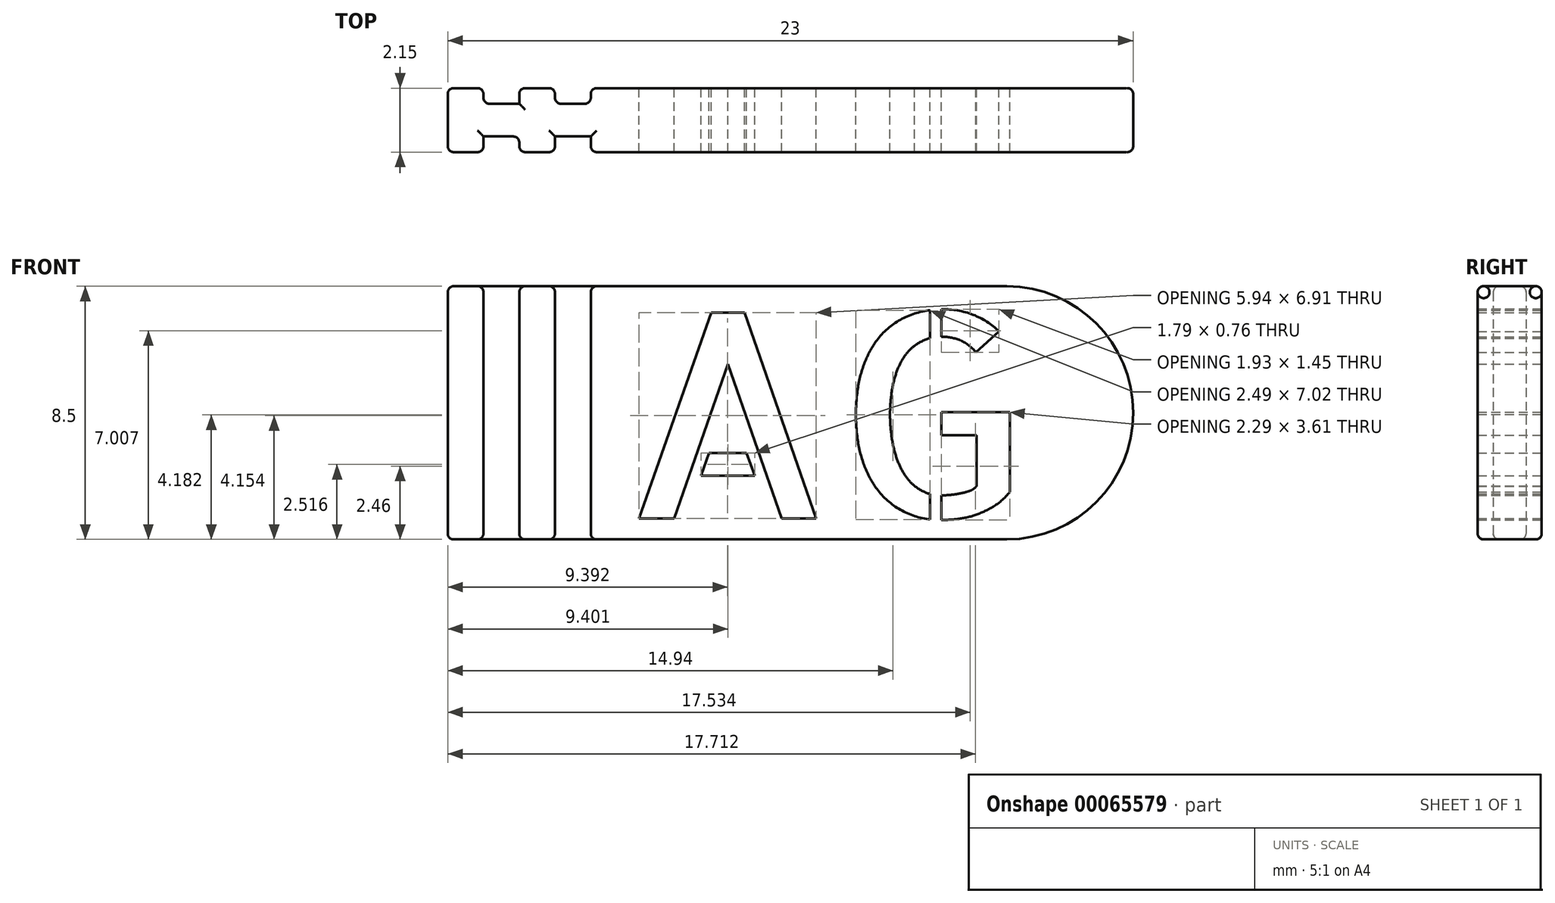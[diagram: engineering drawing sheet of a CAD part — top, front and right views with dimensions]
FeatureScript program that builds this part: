
annotation { "Feature Type Name" : "Feature", "Feature Type Description" : "" }
export const myFeature = defineFeature(function(context is Context, id is Id, definition is map)
    precondition{}
    {
        {
            var Q0;
            Q0=qCreatedBy(makeId("Front.planeOp"),FACE);
            var sketch = newSketch(context, id + "F0", { "sketchPlane" : qUnion([Q0])});
            skLineSegment(sketch, "E0.bottom", {"start": v(0, 0) * mm, "end": v(18.76, 0) * mm});
            skLineSegment(sketch, "E0.top", {"start": v(0, 8.5) * mm, "end": v(18.76, 8.5) * mm});
            skLineSegment(sketch, "E0.left", {"start": v(0, 0) * mm, "end": v(0, 8.5) * mm});
            skPoint(sketch, "E1.third.point", {"position": v(23, 4.25) * mm});
            skArc(sketch, "E2", {"start": v(18.74, 0) * mm, "mid": v(23, 4.25) * mm, "end": v(18.74, 8.5) * mm});
            skLineSegment(sketch, "E3.bottom", {"start": v(0, 8.5) * mm, "end": v(4.8, 8.5) * mm});
            skLineSegment(sketch, "E3.top", {"start": v(0, 0) * mm, "end": v(4.8, 0) * mm});
            skLineSegment(sketch, "E3.left", {"start": v(0, 8.5) * mm, "end": v(0, 0) * mm});
            skLineSegment(sketch, "E3.right", {"start": v(4.8, 8.5) * mm, "end": v(4.8, 0) * mm});
            skLineSegment(sketch, "E4.bottom", {"start": v(0, 8.5) * mm, "end": v(1.2, 8.5) * mm});
            skLineSegment(sketch, "E4.top", {"start": v(0, 0) * mm, "end": v(1.2, 0) * mm});
            skLineSegment(sketch, "E4.right", {"start": v(1.2, 8.5) * mm, "end": v(1.2, 0) * mm});
            skLineSegment(sketch, "E5.bottom", {"start": v(1.2, 8.5) * mm, "end": v(2.4, 8.5) * mm});
            skLineSegment(sketch, "E5.top", {"start": v(1.2, 0) * mm, "end": v(2.4, 0) * mm});
            skLineSegment(sketch, "E5.right", {"start": v(2.4, 8.5) * mm, "end": v(2.4, 0) * mm});
            skLineSegment(sketch, "E6.bottom", {"start": v(2.4, 8.5) * mm, "end": v(3.6, 8.5) * mm});
            skLineSegment(sketch, "E6.top", {"start": v(2.4, 0) * mm, "end": v(3.6, 0) * mm});
            skLineSegment(sketch, "E6.right", {"start": v(3.6, 8.5) * mm, "end": v(3.6, 0) * mm});
            skText(sketch, "E7", { "text": "AG", "fontName": "AllertaStencil-Regular.ttf"});
            const initialGuessF0  = {"E7": [0.00583, 0.0007, 1, 0, 0.00692]};
            skSetInitialGuess(sketch, initialGuessF0);
            skSolve(sketch);
        }
        {
            var Q0;
            {var subQ5=sQuery(id+"F0.wireOp",EDGE,"E3.right");Q0=makeQuery(id+"F0.imprint","IMPRINT",FACE,{"disambiguationData":[TD([[makeQuery(id+"F0.imprint","IMPRINT",EDGE,{"derivedFrom":subQ5}),1.0]])]});}
            extrude(context, id + "F1", {"entities" : qUnion([Q0]), "depth" : 2.15 * mm});
        }
        {
            var Q0;
            Q0=makeQuery(id+"F1.opExtrude","SWEPT_FACE",FACE,{"disambiguationData":[OSD([sQuery(id+"F0.wireOp",EDGE,"E3.right")])]});
            var sketch = newSketch(context, id + "F2", { "sketchPlane" : qUnion([Q0])});
            skLineSegment(sketch, "E8", {"start": v(0, 8.5) * mm, "end": v(2.15, 0) * mm});
            skLineSegment(sketch, "E9.rect.bottom", {"start": v(1.62, 8.5) * mm, "end": v(0.52, 8.5) * mm});
            skLineSegment(sketch, "E9.rect.top", {"start": v(1.62, 0) * mm, "end": v(0.52, 0) * mm});
            skLineSegment(sketch, "E9.rect.left", {"start": v(1.62, 8.5) * mm, "end": v(1.62, 0) * mm});
            skLineSegment(sketch, "E9.rect.right", {"start": v(0.52, 8.5) * mm, "end": v(0.52, 0) * mm});
            skPoint(sketch, "E9.rect.middle", {"position": v(1.07, 4.25) * mm});
            skSolve(sketch);
        }
        {
            var Q0;
            {var subQ5=sQuery(id+"F2.wireOp",EDGE,"E9.rect.bottom");Q0=makeQuery(id+"F2.imprint","IMPRINT",FACE,{"disambiguationData":[TD([[makeQuery(id+"F2.imprint","IMPRINT",EDGE,{"derivedFrom":subQ5}),1.0]])]});}
            var Q1;
            {var subQ5=sQuery(id+"F2.wireOp",EDGE,"E9.rect.top");Q1=makeQuery(id+"F2.imprint","IMPRINT",FACE,{"disambiguationData":[TD([[makeQuery(id+"F2.imprint","IMPRINT",EDGE,{"derivedFrom":subQ5}),-1.0]])]});}
            extrude(context, id + "F3", {"entities" : qUnion([Q0, Q1]), "operationType" : NewBodyOperationType.ADD, "depth" : 1.2 * mm});
        }
        {
            var Q0;
            Q0=makeQuery(id+"F3.opExtrude","CAP_FACE",FACE,{"disambiguationData":[OSD([sQuery(id+"F2.wireOp",EDGE,"E9.rect.bottom"),sQuery(id+"F2.wireOp",EDGE,"E9.rect.top"),sQuery(id+"F2.wireOp",EDGE,"E9.rect.left"),sQuery(id+"F2.wireOp",EDGE,"E9.rect.right")])],"isStart":false});
            var sketch = newSketch(context, id + "F4", { "sketchPlane" : qUnion([Q0])});
            skLineSegment(sketch, "E10.bottom", {"start": v(0, 0) * mm, "end": v(2.15, 0) * mm});
            skLineSegment(sketch, "E10.top", {"start": v(0, 8.5) * mm, "end": v(2.15, 8.5) * mm});
            skLineSegment(sketch, "E10.left", {"start": v(0, 0) * mm, "end": v(0, 8.5) * mm});
            skLineSegment(sketch, "E10.right", {"start": v(2.15, 0) * mm, "end": v(2.15, 8.5) * mm});
            skSolve(sketch);
        }
        {
            var Q0;
            {var subQ2=sQuery(id+"F4.wireOp",EDGE,"E10.right");Q0=makeQuery(id+"F4.imprint","IMPRINT",FACE,{"disambiguationData":[TD([[makeQuery(id+"F4.imprint","IMPRINT",EDGE,{"derivedFrom":subQ2}),1.0]])]});}
            var Q1;
            {var subQ1=makeQuery(id+"F3.opExtrude","CAP_EDGE",EDGE,{"disambiguationData":[OSD([sQuery(id+"F2.wireOp",EDGE,"E9.rect.left")])],"isStart":false});Q1=makeQuery(id+"F4.imprint","IMPRINT",FACE,{"disambiguationData":[TD([[makeQuery(id+"F4.imprint","IMPRINT",EDGE,{"derivedFrom":subQ1}),-1.0]])]});}
            var Q2;
            {var subQ2=sQuery(id+"F4.wireOp",EDGE,"E10.left");Q2=makeQuery(id+"F4.imprint","IMPRINT",FACE,{"disambiguationData":[TD([[makeQuery(id+"F4.imprint","IMPRINT",EDGE,{"derivedFrom":subQ2}),-1.0]])]});}
            extrude(context, id + "F5", {"entities" : qUnion([Q0, Q1, Q2]), "operationType" : NewBodyOperationType.ADD, "depth" : 1.2 * mm});
        }
        {
            var Q0;
            Q0=makeQuery(id+"F5.opExtrude","CAP_FACE",FACE,{"disambiguationData":[OSD([sQuery(id+"F4.wireOp",EDGE,"E10.bottom"),sQuery(id+"F4.wireOp",EDGE,"E10.top"),sQuery(id+"F4.wireOp",EDGE,"E10.left"),sQuery(id+"F4.wireOp",EDGE,"E10.right")])],"isStart":false});
            var sketch = newSketch(context, id + "F6", { "sketchPlane" : qUnion([Q0])});
            skLineSegment(sketch, "E11", {"start": v(0, 0) * mm, "end": v(2.15, 8.5) * mm});
            skLineSegment(sketch, "E12.rect.bottom", {"start": v(1.63, 8.5) * mm, "end": v(0.53, 8.5) * mm});
            skLineSegment(sketch, "E12.rect.top", {"start": v(1.63, 0) * mm, "end": v(0.53, 0) * mm});
            skLineSegment(sketch, "E12.rect.left", {"start": v(1.63, 8.5) * mm, "end": v(1.63, 0) * mm});
            skLineSegment(sketch, "E12.rect.right", {"start": v(0.53, 8.5) * mm, "end": v(0.53, 0) * mm});
            skPoint(sketch, "E12.rect.middle", {"position": v(1.07, 4.25) * mm});
            skSolve(sketch);
        }
        {
            var Q0;
            {var subQ5=sQuery(id+"F6.wireOp",EDGE,"E12.rect.top");Q0=makeQuery(id+"F6.imprint","IMPRINT",FACE,{"disambiguationData":[TD([[makeQuery(id+"F6.imprint","IMPRINT",EDGE,{"derivedFrom":subQ5}),1.0]])]});}
            var Q1;
            {var subQ5=sQuery(id+"F6.wireOp",EDGE,"E12.rect.bottom");Q1=makeQuery(id+"F6.imprint","IMPRINT",FACE,{"disambiguationData":[TD([[makeQuery(id+"F6.imprint","IMPRINT",EDGE,{"derivedFrom":subQ5}),-1.0]])]});}
            extrude(context, id + "F7", {"entities" : qUnion([Q0, Q1]), "operationType" : NewBodyOperationType.ADD, "depth" : 1.2 * mm});
        }
        {
            var Q0;
            Q0=makeQuery(id+"F7.opExtrude","CAP_FACE",FACE,{"disambiguationData":[OSD([sQuery(id+"F6.wireOp",EDGE,"E12.rect.bottom"),sQuery(id+"F6.wireOp",EDGE,"E12.rect.top"),sQuery(id+"F6.wireOp",EDGE,"E12.rect.left"),sQuery(id+"F6.wireOp",EDGE,"E12.rect.right")])],"isStart":false});
            var sketch = newSketch(context, id + "F8", { "sketchPlane" : qUnion([Q0])});
            skLineSegment(sketch, "E13.bottom", {"start": v(0, 0) * mm, "end": v(2.15, 0) * mm});
            skLineSegment(sketch, "E13.top", {"start": v(0, 8.5) * mm, "end": v(2.15, 8.5) * mm});
            skLineSegment(sketch, "E13.left", {"start": v(0, 0) * mm, "end": v(0, 8.5) * mm});
            skLineSegment(sketch, "E13.right", {"start": v(2.15, 0) * mm, "end": v(2.15, 8.5) * mm});
            skSolve(sketch);
        }
        {
            var Q0;
            {var subQ2=makeQuery(id+"F7.opExtrude","CAP_EDGE",EDGE,{"disambiguationData":[OSD([sQuery(id+"F6.wireOp",EDGE,"E12.rect.left")])],"isStart":false});Q0=makeQuery(id+"F8.imprint","IMPRINT",FACE,{"disambiguationData":[TD([[makeQuery(id+"F8.imprint","IMPRINT",EDGE,{"derivedFrom":subQ2}),-1.0]])]});}
            var Q1;
            {var subQ2=sQuery(id+"F8.wireOp",EDGE,"E13.left");Q1=makeQuery(id+"F8.imprint","IMPRINT",FACE,{"disambiguationData":[TD([[makeQuery(id+"F8.imprint","IMPRINT",EDGE,{"derivedFrom":subQ2}),-1.0]])]});}
            var Q2;
            {var subQ2=sQuery(id+"F8.wireOp",EDGE,"E13.right");Q2=makeQuery(id+"F8.imprint","IMPRINT",FACE,{"disambiguationData":[TD([[makeQuery(id+"F8.imprint","IMPRINT",EDGE,{"derivedFrom":subQ2}),1.0]])]});}
            extrude(context, id + "F9", {"entities" : qUnion([Q0, Q1, Q2]), "operationType" : NewBodyOperationType.ADD, "depth" : 1.2 * mm});
        }
        {
            var Q0;
            Q0=makeQuery(id+"F1.opExtrude","CAP_EDGE",EDGE,{"disambiguationData":[OSD([sQuery(id+"F0.wireOp",EDGE,"E0.top")])],"isStart":false});
            var Q1;
            Q1=makeQuery(id+"F1.opExtrude","CAP_EDGE",EDGE,{"disambiguationData":[OSD([sQuery(id+"F0.wireOp",EDGE,"E2")])],"isStart":false});
            var Q2;
            Q2=makeQuery(id+"F1.opExtrude","CAP_EDGE",EDGE,{"disambiguationData":[OSD([sQuery(id+"F0.wireOp",EDGE,"E0.bottom")])],"isStart":false});
            var Q3;
            Q3=makeQuery(id+"F1.opExtrude","CAP_EDGE",EDGE,{"disambiguationData":[OSD([sQuery(id+"F0.wireOp",EDGE,"E3.right")])],"isStart":false});
            var Q4;
            Q4=makeQuery(id+"F1.opExtrude","CAP_EDGE",EDGE,{"disambiguationData":[OSD([sQuery(id+"F0.wireOp",EDGE,"E0.top")])],"isStart":true});
            var Q5;
            Q5=makeQuery(id+"F1.opExtrude","CAP_EDGE",EDGE,{"disambiguationData":[OSD([sQuery(id+"F0.wireOp",EDGE,"E2")])],"isStart":true});
            var Q6;
            Q6=makeQuery(id+"F1.opExtrude","CAP_EDGE",EDGE,{"disambiguationData":[OSD([sQuery(id+"F0.wireOp",EDGE,"E0.bottom")])],"isStart":true});
            var Q7;
            Q7=makeQuery(id+"F1.opExtrude","CAP_EDGE",EDGE,{"disambiguationData":[OSD([sQuery(id+"F0.wireOp",EDGE,"E3.right")])],"isStart":true});
            var Q8;
            Q8=makeQuery(id+"F5.opExtrude","CAP_EDGE",EDGE,{"disambiguationData":[OSD([sQuery(id+"F4.wireOp",EDGE,"E10.left")])],"isStart":true});
            var Q9;
            Q9=makeQuery(id+"F5.opExtrude","SWEPT_EDGE",EDGE,{"disambiguationData":[OSD([sQuery(id+"F4.wireOp",EDGE,"E10.bottom"),sQuery(id+"F4.wireOp",EDGE,"E10.left")])]});
            var Q10;
            Q10=makeQuery(id+"F5.opExtrude","CAP_EDGE",EDGE,{"disambiguationData":[OSD([sQuery(id+"F4.wireOp",EDGE,"E10.left")])],"isStart":false});
            var Q11;
            Q11=makeQuery(id+"F5.opExtrude","SWEPT_EDGE",EDGE,{"disambiguationData":[OSD([sQuery(id+"F4.wireOp",EDGE,"E10.top"),sQuery(id+"F4.wireOp",EDGE,"E10.left")])]});
            var Q12;
            Q12=makeQuery(id+"F9.opExtrude","CAP_EDGE",EDGE,{"disambiguationData":[OSD([sQuery(id+"F8.wireOp",EDGE,"E13.left")])],"isStart":true});
            var Q13;
            Q13=makeQuery(id+"F9.opExtrude","SWEPT_EDGE",EDGE,{"disambiguationData":[OSD([sQuery(id+"F8.wireOp",EDGE,"E13.bottom"),sQuery(id+"F8.wireOp",EDGE,"E13.left")])]});
            var Q14;
            Q14=makeQuery(id+"F9.opExtrude","CAP_EDGE",EDGE,{"disambiguationData":[OSD([sQuery(id+"F8.wireOp",EDGE,"E13.left")])],"isStart":false});
            var Q15;
            Q15=makeQuery(id+"F9.opExtrude","SWEPT_EDGE",EDGE,{"disambiguationData":[OSD([sQuery(id+"F8.wireOp",EDGE,"E13.top"),sQuery(id+"F8.wireOp",EDGE,"E13.left")])]});
            var Q16;
            Q16=makeQuery(id+"F5.opExtrude","CAP_EDGE",EDGE,{"disambiguationData":[OSD([sQuery(id+"F4.wireOp",EDGE,"E10.right")])],"isStart":true});
            var Q17;
            Q17=makeQuery(id+"F5.opExtrude","CAP_EDGE",EDGE,{"disambiguationData":[OSD([sQuery(id+"F4.wireOp",EDGE,"E10.right")])],"isStart":false});
            var Q18;
            Q18=makeQuery(id+"F9.opExtrude","CAP_EDGE",EDGE,{"disambiguationData":[OSD([sQuery(id+"F8.wireOp",EDGE,"E13.right")])],"isStart":true});
            var Q19;
            Q19=makeQuery(id+"F9.opExtrude","SWEPT_EDGE",EDGE,{"disambiguationData":[OSD([sQuery(id+"F8.wireOp",EDGE,"E13.bottom"),sQuery(id+"F8.wireOp",EDGE,"E13.right")])]});
            var Q20;
            Q20=makeQuery(id+"F9.opExtrude","CAP_EDGE",EDGE,{"disambiguationData":[OSD([sQuery(id+"F8.wireOp",EDGE,"E13.right")])],"isStart":false});
            var Q21;
            Q21=makeQuery(id+"F9.opExtrude","SWEPT_EDGE",EDGE,{"disambiguationData":[OSD([sQuery(id+"F8.wireOp",EDGE,"E13.top"),sQuery(id+"F8.wireOp",EDGE,"E13.right")])]});
            var Q22;
            Q22=makeQuery(id+"F3.opExtrude","CAP_EDGE",EDGE,{"disambiguationData":[OSD([sQuery(id+"F2.wireOp",EDGE,"E9.rect.left")])],"isStart":false});
            var Q23;
            Q23=makeQuery(id+"F7.opExtrude","CAP_EDGE",EDGE,{"disambiguationData":[OSD([sQuery(id+"F6.wireOp",EDGE,"E12.rect.left")])],"isStart":false});
            var Q24;
            {var subQ1=sQuery(id+"F8.wireOp",EDGE,"E13.bottom");Q24=makeQuery(id+"F9.boolean.opBoolean","SPLIT",EDGE,{"disambiguationData":[TD([makeQuery(id+"F7.opExtrude","SWEPT_FACE",FACE,{"disambiguationData":[OSD([sQuery(id+"F6.wireOp",EDGE,"E12.rect.left")])]})])],"derivedFrom":makeQuery(id+"F9.opExtrude","CAP_EDGE",EDGE,{"disambiguationData":[OSD([subQ1])],"isStart":true})});}
            var Q25;
            {var subQ0=sQuery(id+"F4.wireOp",EDGE,"E10.right");var subQ1=sQuery(id+"F4.wireOp",EDGE,"E10.bottom");Q25=makeQuery(id+"F7.boolean.opBoolean","SPLIT",EDGE,{"disambiguationData":[TD([makeQuery(id+"F5.opExtrude","SWEPT_FACE",FACE,{"disambiguationData":[OSD([subQ0])]})])],"derivedFrom":makeQuery(id+"F5.opExtrude","CAP_EDGE",EDGE,{"disambiguationData":[OSD([subQ1])],"isStart":false})});}
            var Q26;
            {var subQ0=sQuery(id+"F4.wireOp",EDGE,"E10.bottom");Q26=makeQuery(id+"F5.boolean.opBoolean","SPLIT",EDGE,{"disambiguationData":[TD([makeQuery(id+"F3.opExtrude","SWEPT_FACE",FACE,{"disambiguationData":[OSD([sQuery(id+"F2.wireOp",EDGE,"E9.rect.left")])]})])],"derivedFrom":makeQuery(id+"F5.opExtrude","CAP_EDGE",EDGE,{"disambiguationData":[OSD([subQ0])],"isStart":true})});}
            var Q27;
            Q27=makeQuery(id+"F3.opExtrude","SWEPT_EDGE",EDGE,{"disambiguationData":[OSD([sQuery(id+"F0.wireOp",EDGE,"E0.bottom"),sQuery(id+"F0.wireOp",EDGE,"E3.top"),sQuery(id+"F0.wireOp",EDGE,"E3.right"),sQuery(id+"F2.wireOp",EDGE,"E9.rect.top"),sQuery(id+"F2.wireOp",EDGE,"E9.rect.left")])]});
            var Q28;
            {var subQ0=sQuery(id+"F0.wireOp",EDGE,"E3.right");var subQ1=sQuery(id+"F0.wireOp",EDGE,"E0.bottom");Q28=makeQuery(id+"F3.boolean.opBoolean","SPLIT",EDGE,{"disambiguationData":[TD([makeQuery(id+"F3.opExtrude","SWEPT_FACE",FACE,{"disambiguationData":[OSD([sQuery(id+"F2.wireOp",EDGE,"E9.rect.left")])]})])],"derivedFrom":makeQuery(id+"F1.opExtrude","SWEPT_EDGE",EDGE,{"disambiguationData":[OSD([subQ1,sQuery(id+"F0.wireOp",EDGE,"E3.top"),subQ0])]})});}
            var Q29;
            {var subQ0=sQuery(id+"F4.wireOp",EDGE,"E10.bottom");Q29=makeQuery(id+"F5.boolean.opBoolean","SPLIT",EDGE,{"disambiguationData":[TD([makeQuery(id+"F3.opExtrude","SWEPT_FACE",FACE,{"disambiguationData":[OSD([sQuery(id+"F2.wireOp",EDGE,"E9.rect.right")])]})])],"derivedFrom":makeQuery(id+"F5.opExtrude","CAP_EDGE",EDGE,{"disambiguationData":[OSD([subQ0])],"isStart":true})});}
            var Q30;
            Q30=makeQuery(id+"F3.opExtrude","SWEPT_EDGE",EDGE,{"disambiguationData":[OSD([sQuery(id+"F0.wireOp",EDGE,"E0.bottom"),sQuery(id+"F0.wireOp",EDGE,"E3.top"),sQuery(id+"F0.wireOp",EDGE,"E3.right"),sQuery(id+"F2.wireOp",EDGE,"E9.rect.top"),sQuery(id+"F2.wireOp",EDGE,"E9.rect.right")])]});
            var Q31;
            {var subQ0=sQuery(id+"F0.wireOp",EDGE,"E3.right");var subQ1=sQuery(id+"F0.wireOp",EDGE,"E0.bottom");Q31=makeQuery(id+"F3.boolean.opBoolean","SPLIT",EDGE,{"disambiguationData":[TD([makeQuery(id+"F3.opExtrude","SWEPT_FACE",FACE,{"disambiguationData":[OSD([sQuery(id+"F2.wireOp",EDGE,"E9.rect.right")])]})])],"derivedFrom":makeQuery(id+"F1.opExtrude","SWEPT_EDGE",EDGE,{"disambiguationData":[OSD([subQ1,sQuery(id+"F0.wireOp",EDGE,"E3.top"),subQ0])]})});}
            var Q32;
            Q32=makeQuery(id+"F9.opExtrude","CAP_EDGE",EDGE,{"disambiguationData":[OSD([sQuery(id+"F8.wireOp",EDGE,"E13.bottom")])],"isStart":false});
            var Q33;
            {var subQ1=sQuery(id+"F8.wireOp",EDGE,"E13.bottom");Q33=makeQuery(id+"F9.boolean.opBoolean","SPLIT",EDGE,{"disambiguationData":[TD([makeQuery(id+"F7.opExtrude","SWEPT_FACE",FACE,{"disambiguationData":[OSD([sQuery(id+"F6.wireOp",EDGE,"E12.rect.right")])]})])],"derivedFrom":makeQuery(id+"F9.opExtrude","CAP_EDGE",EDGE,{"disambiguationData":[OSD([subQ1])],"isStart":true})});}
            var Q34;
            Q34=makeQuery(id+"F7.opExtrude","SWEPT_EDGE",EDGE,{"disambiguationData":[OSD([sQuery(id+"F4.wireOp",EDGE,"E10.bottom"),sQuery(id+"F6.wireOp",EDGE,"E12.rect.top"),sQuery(id+"F6.wireOp",EDGE,"E12.rect.right")])]});
            var Q35;
            {var subQ0=sQuery(id+"F4.wireOp",EDGE,"E10.left");var subQ1=sQuery(id+"F4.wireOp",EDGE,"E10.bottom");Q35=makeQuery(id+"F7.boolean.opBoolean","SPLIT",EDGE,{"disambiguationData":[TD([makeQuery(id+"F5.opExtrude","SWEPT_FACE",FACE,{"disambiguationData":[OSD([subQ0])]})])],"derivedFrom":makeQuery(id+"F5.opExtrude","CAP_EDGE",EDGE,{"disambiguationData":[OSD([subQ1])],"isStart":false})});}
            var Q36;
            Q36=makeQuery(id+"F3.opExtrude","CAP_EDGE",EDGE,{"disambiguationData":[OSD([sQuery(id+"F2.wireOp",EDGE,"E9.rect.left")])],"isStart":true});
            var Q37;
            Q37=makeQuery(id+"F7.opExtrude","CAP_EDGE",EDGE,{"disambiguationData":[OSD([sQuery(id+"F6.wireOp",EDGE,"E12.rect.left")])],"isStart":true});
            var Q38;
            Q38=makeQuery(id+"F3.opExtrude","CAP_EDGE",EDGE,{"disambiguationData":[OSD([sQuery(id+"F2.wireOp",EDGE,"E9.rect.right")])],"isStart":true});
            var Q39;
            Q39=makeQuery(id+"F7.opExtrude","CAP_EDGE",EDGE,{"disambiguationData":[OSD([sQuery(id+"F6.wireOp",EDGE,"E12.rect.right")])],"isStart":true});
            var Q40;
            Q40=makeQuery(id+"F7.opExtrude","CAP_EDGE",EDGE,{"disambiguationData":[OSD([sQuery(id+"F6.wireOp",EDGE,"E12.rect.right")])],"isStart":false});
            var Q41;
            Q41=makeQuery(id+"F7.opExtrude","SWEPT_EDGE",EDGE,{"disambiguationData":[OSD([sQuery(id+"F4.wireOp",EDGE,"E10.top"),sQuery(id+"F6.wireOp",EDGE,"E12.rect.bottom"),sQuery(id+"F6.wireOp",EDGE,"E12.rect.right")])]});
            var Q42;
            Q42=makeQuery(id+"F3.opExtrude","SWEPT_EDGE",EDGE,{"disambiguationData":[OSD([sQuery(id+"F0.wireOp",EDGE,"E0.top"),sQuery(id+"F0.wireOp",EDGE,"E3.bottom"),sQuery(id+"F0.wireOp",EDGE,"E3.right"),sQuery(id+"F2.wireOp",EDGE,"E9.rect.bottom"),sQuery(id+"F2.wireOp",EDGE,"E9.rect.right")])]});
            var Q43;
            Q43=makeQuery(id+"F3.opExtrude","CAP_EDGE",EDGE,{"disambiguationData":[OSD([sQuery(id+"F2.wireOp",EDGE,"E9.rect.right")])],"isStart":false});
            var Q44;
            Q44=makeQuery(id+"F3.opExtrude","SWEPT_EDGE",EDGE,{"disambiguationData":[OSD([sQuery(id+"F0.wireOp",EDGE,"E0.top"),sQuery(id+"F0.wireOp",EDGE,"E3.bottom"),sQuery(id+"F0.wireOp",EDGE,"E3.right"),sQuery(id+"F2.wireOp",EDGE,"E9.rect.bottom"),sQuery(id+"F2.wireOp",EDGE,"E9.rect.left")])]});
            var Q45;
            Q45=makeQuery(id+"F7.opExtrude","SWEPT_EDGE",EDGE,{"disambiguationData":[OSD([sQuery(id+"F4.wireOp",EDGE,"E10.top"),sQuery(id+"F6.wireOp",EDGE,"E12.rect.bottom"),sQuery(id+"F6.wireOp",EDGE,"E12.rect.left")])]});
            var Q46;
            Q46=makeQuery(id+"F5.opExtrude","SWEPT_EDGE",EDGE,{"disambiguationData":[OSD([sQuery(id+"F4.wireOp",EDGE,"E10.bottom"),sQuery(id+"F4.wireOp",EDGE,"E10.right")])]});
            var Q47;
            Q47=makeQuery(id+"F9.opExtrude","CAP_EDGE",EDGE,{"disambiguationData":[OSD([sQuery(id+"F8.wireOp",EDGE,"E13.top")])],"isStart":false});
            var Q48;
            {var subQ0=sQuery(id+"F4.wireOp",EDGE,"E10.top");var subQ1=sQuery(id+"F4.wireOp",EDGE,"E10.right");Q48=makeQuery(id+"F7.boolean.opBoolean","SPLIT",EDGE,{"disambiguationData":[TD([makeQuery(id+"F5.opExtrude","SWEPT_FACE",FACE,{"disambiguationData":[OSD([subQ1])]})])],"derivedFrom":makeQuery(id+"F5.opExtrude","CAP_EDGE",EDGE,{"disambiguationData":[OSD([subQ0])],"isStart":false})});}
            var Q49;
            {var subQ1=sQuery(id+"F8.wireOp",EDGE,"E13.top");Q49=makeQuery(id+"F9.boolean.opBoolean","SPLIT",EDGE,{"disambiguationData":[TD([makeQuery(id+"F7.opExtrude","SWEPT_FACE",FACE,{"disambiguationData":[OSD([sQuery(id+"F6.wireOp",EDGE,"E12.rect.left")])]})])],"derivedFrom":makeQuery(id+"F9.opExtrude","CAP_EDGE",EDGE,{"disambiguationData":[OSD([subQ1])],"isStart":true})});}
            var Q50;
            {var subQ1=sQuery(id+"F4.wireOp",EDGE,"E10.top");Q50=makeQuery(id+"F5.boolean.opBoolean","SPLIT",EDGE,{"disambiguationData":[TD([makeQuery(id+"F3.opExtrude","SWEPT_FACE",FACE,{"disambiguationData":[OSD([sQuery(id+"F2.wireOp",EDGE,"E9.rect.left")])]})])],"derivedFrom":makeQuery(id+"F5.opExtrude","CAP_EDGE",EDGE,{"disambiguationData":[OSD([subQ1])],"isStart":true})});}
            var Q51;
            Q51=makeQuery(id+"F5.opExtrude","SWEPT_EDGE",EDGE,{"disambiguationData":[OSD([sQuery(id+"F4.wireOp",EDGE,"E10.top"),sQuery(id+"F4.wireOp",EDGE,"E10.right")])]});
            var Q52;
            {var subQ1=sQuery(id+"F8.wireOp",EDGE,"E13.top");Q52=makeQuery(id+"F9.boolean.opBoolean","SPLIT",EDGE,{"disambiguationData":[TD([makeQuery(id+"F7.opExtrude","SWEPT_FACE",FACE,{"disambiguationData":[OSD([sQuery(id+"F6.wireOp",EDGE,"E12.rect.right")])]})])],"derivedFrom":makeQuery(id+"F9.opExtrude","CAP_EDGE",EDGE,{"disambiguationData":[OSD([subQ1])],"isStart":true})});}
            var Q53;
            {var subQ0=sQuery(id+"F4.wireOp",EDGE,"E10.left");var subQ1=sQuery(id+"F4.wireOp",EDGE,"E10.top");Q53=makeQuery(id+"F7.boolean.opBoolean","SPLIT",EDGE,{"disambiguationData":[TD([makeQuery(id+"F5.opExtrude","SWEPT_FACE",FACE,{"disambiguationData":[OSD([subQ0])]})])],"derivedFrom":makeQuery(id+"F5.opExtrude","CAP_EDGE",EDGE,{"disambiguationData":[OSD([subQ1])],"isStart":false})});}
            var Q54;
            {var subQ1=sQuery(id+"F4.wireOp",EDGE,"E10.top");Q54=makeQuery(id+"F5.boolean.opBoolean","SPLIT",EDGE,{"disambiguationData":[TD([makeQuery(id+"F3.opExtrude","SWEPT_FACE",FACE,{"disambiguationData":[OSD([sQuery(id+"F2.wireOp",EDGE,"E9.rect.right")])]})])],"derivedFrom":makeQuery(id+"F5.opExtrude","CAP_EDGE",EDGE,{"disambiguationData":[OSD([subQ1])],"isStart":true})});}
            var Q55;
            {var subQ0=sQuery(id+"F0.wireOp",EDGE,"E3.right");var subQ1=sQuery(id+"F0.wireOp",EDGE,"E0.top");Q55=makeQuery(id+"F3.boolean.opBoolean","SPLIT",EDGE,{"disambiguationData":[TD([makeQuery(id+"F3.opExtrude","SWEPT_FACE",FACE,{"disambiguationData":[OSD([sQuery(id+"F2.wireOp",EDGE,"E9.rect.left")])]})])],"derivedFrom":makeQuery(id+"F1.opExtrude","SWEPT_EDGE",EDGE,{"disambiguationData":[OSD([subQ1,sQuery(id+"F0.wireOp",EDGE,"E3.bottom"),subQ0])]})});}
            var Q56;
            {var subQ0=sQuery(id+"F0.wireOp",EDGE,"E3.right");var subQ1=sQuery(id+"F0.wireOp",EDGE,"E0.top");Q56=makeQuery(id+"F3.boolean.opBoolean","SPLIT",EDGE,{"disambiguationData":[TD([makeQuery(id+"F3.opExtrude","SWEPT_FACE",FACE,{"disambiguationData":[OSD([sQuery(id+"F2.wireOp",EDGE,"E9.rect.right")])]})])],"derivedFrom":makeQuery(id+"F1.opExtrude","SWEPT_EDGE",EDGE,{"disambiguationData":[OSD([subQ1,sQuery(id+"F0.wireOp",EDGE,"E3.bottom"),subQ0])]})});}
            var Q57;
            Q57=makeQuery(id+"F7.opExtrude","SWEPT_EDGE",EDGE,{"disambiguationData":[OSD([sQuery(id+"F4.wireOp",EDGE,"E10.bottom"),sQuery(id+"F6.wireOp",EDGE,"E12.rect.top"),sQuery(id+"F6.wireOp",EDGE,"E12.rect.left")])]});
            fillet(context, id + "F10", {"entities" : qUnion([Q0, Q1, Q2, Q3, Q4, Q5, Q6, Q7, Q8, Q9, Q10, Q11, Q12, Q13, Q14, Q15, Q16, Q17, Q18, Q19, Q20, Q21, Q22, Q23, Q24, Q25, Q26, Q27, Q28, Q29, Q30, Q31, Q32, Q33, Q34, Q35, Q36, Q37, Q38, Q39, Q40, Q41, Q42, Q43, Q44, Q45, Q46, Q47, Q48, Q49, Q50, Q51, Q52, Q53, Q54, Q55, Q56, Q57]), "radius" : 0.2 * mm, "tangentPropagation" : true, "allowEdgeOverflow" : false});
        }
    });
